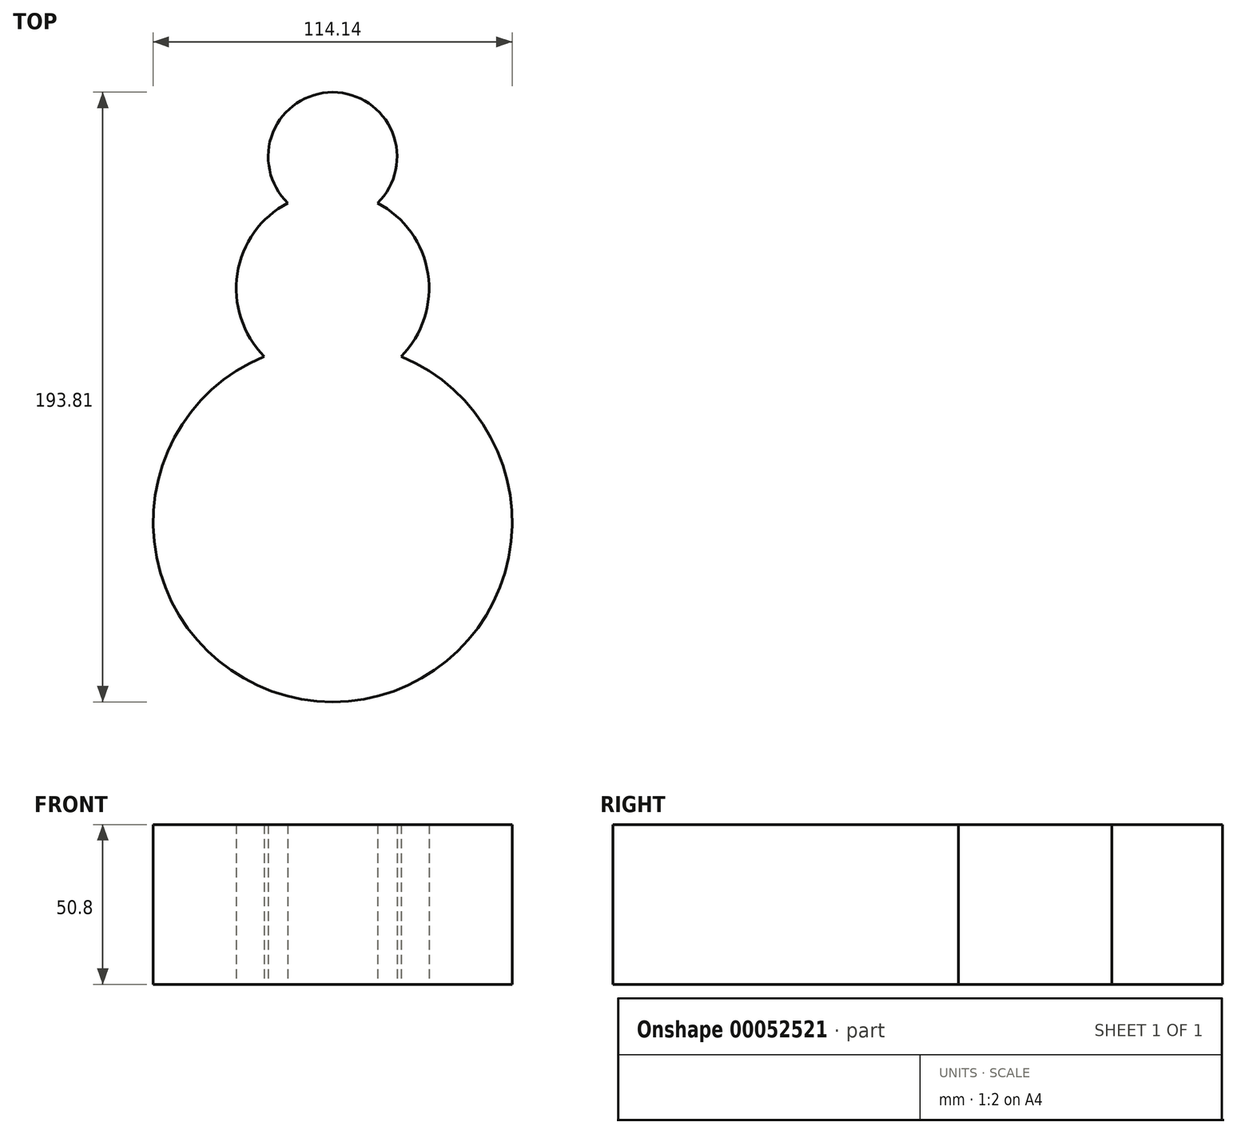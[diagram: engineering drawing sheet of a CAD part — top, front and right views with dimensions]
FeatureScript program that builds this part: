
annotation { "Feature Type Name" : "Feature", "Feature Type Description" : "" }
export const myFeature = defineFeature(function(context is Context, id is Id, definition is map)
    precondition{}
    {
        {
            var Q0;
            Q0=qCreatedBy(makeId("Top.planeOp"),FACE);
            var sketch = newSketch(context, id + "F0", { "sketchPlane" : qUnion([Q0])});
            skArc(sketch, "E0", {"start": v(14.24, -14.73) * mm, "mid": v(0, 20.49) * mm, "end": v(-14.24, -14.73) * mm});
            skArc(sketch, "E1", {"start": v(-14.24, -14.73) * mm, "mid": v(-30.3, -37.22) * mm, "end": v(-21.75, -63.5) * mm});
            skArc(sketch, "E2", {"start": v(-21.75, -63.5) * mm, "mid": v(0, -173.32) * mm, "end": v(21.75, -63.5) * mm});
            skArc(sketch, "E3.trimOffspring", {"start": v(21.75, -63.5) * mm, "mid": v(30.3, -37.22) * mm, "end": v(14.24, -14.73) * mm});
            skSolve(sketch);
        }
        {
            var Q0;
            Q0 = qSketchRegion(id + "F0", true);
            extrude(context, id + "F1", {"entities" : qUnion([Q0]), "depth" : 25.4 * mm});
        }
        {
            var Q0;
            Q0=makeQuery(id+"F1.opExtrude","CAP_FACE",FACE,{"disambiguationData":[OSD([sQuery(id+"F0.wireOp",EDGE,"E0"),sQuery(id+"F0.wireOp",EDGE,"E1"),sQuery(id+"F0.wireOp",EDGE,"E2"),sQuery(id+"F0.wireOp",EDGE,"E3.trimOffspring")])],"isStart":false});
            var sketch = newSketch(context, id + "F2", { "sketchPlane" : qUnion([Q0])});
            skCircle(sketch, "E4", {"center": v(-16.63, 0) * mm, "radius": 3.18 * mm});
            skCircle(sketch, "E5", {"center": v(10.2, 0) * mm, "radius": 4.36 * mm});
            skSolve(sketch);
        }
        {
            var Q0;
            Q0=makeQuery(id+"F2.imprint","IMPRINT",FACE,{"disambiguationData":[TD([[makeQuery(id+"F2.imprint","IMPRINT",EDGE,{"derivedFrom":sQuery(id+"F2.wireOp",EDGE,"E4")}),1.0]])]});
            var Q1;
            Q1=makeQuery(id+"F2.imprint","IMPRINT",FACE,{"disambiguationData":[TD([[makeQuery(id+"F2.imprint","IMPRINT",EDGE,{"derivedFrom":sQuery(id+"F2.wireOp",EDGE,"E5")}),1.0]])]});
            var Q2;
            Q2=makeQuery(id+"F1.opExtrude","CAP_FACE",FACE,{"disambiguationData":[OSD([sQuery(id+"F0.wireOp",EDGE,"E0"),sQuery(id+"F0.wireOp",EDGE,"E1"),sQuery(id+"F0.wireOp",EDGE,"E2"),sQuery(id+"F0.wireOp",EDGE,"E3.trimOffspring")])],"isStart":false});
            var Q3;
            Q3=makeQuery(id+"F1.opExtrude","CAP_FACE",FACE,{"disambiguationData":[OSD([sQuery(id+"F0.wireOp",EDGE,"E0"),sQuery(id+"F0.wireOp",EDGE,"E1"),sQuery(id+"F0.wireOp",EDGE,"E2"),sQuery(id+"F0.wireOp",EDGE,"E3.trimOffspring")])],"isStart":true});
            var Q4;
            Q4=makeQuery(id+"F2.imprint","IMPRINT",FACE,{"disambiguationData":[TD([[makeQuery(id+"F2.imprint","IMPRINT",EDGE,{"derivedFrom":sQuery(id+"F2.wireOp",EDGE,"E4")}),-1.0]])]});
            extrude(context, id + "F3", {"entities" : qUnion([Q0, Q1, Q2, Q3, Q4]), "operationType" : NewBodyOperationType.ADD, "depth" : 25.4 * mm});
        }
    });
